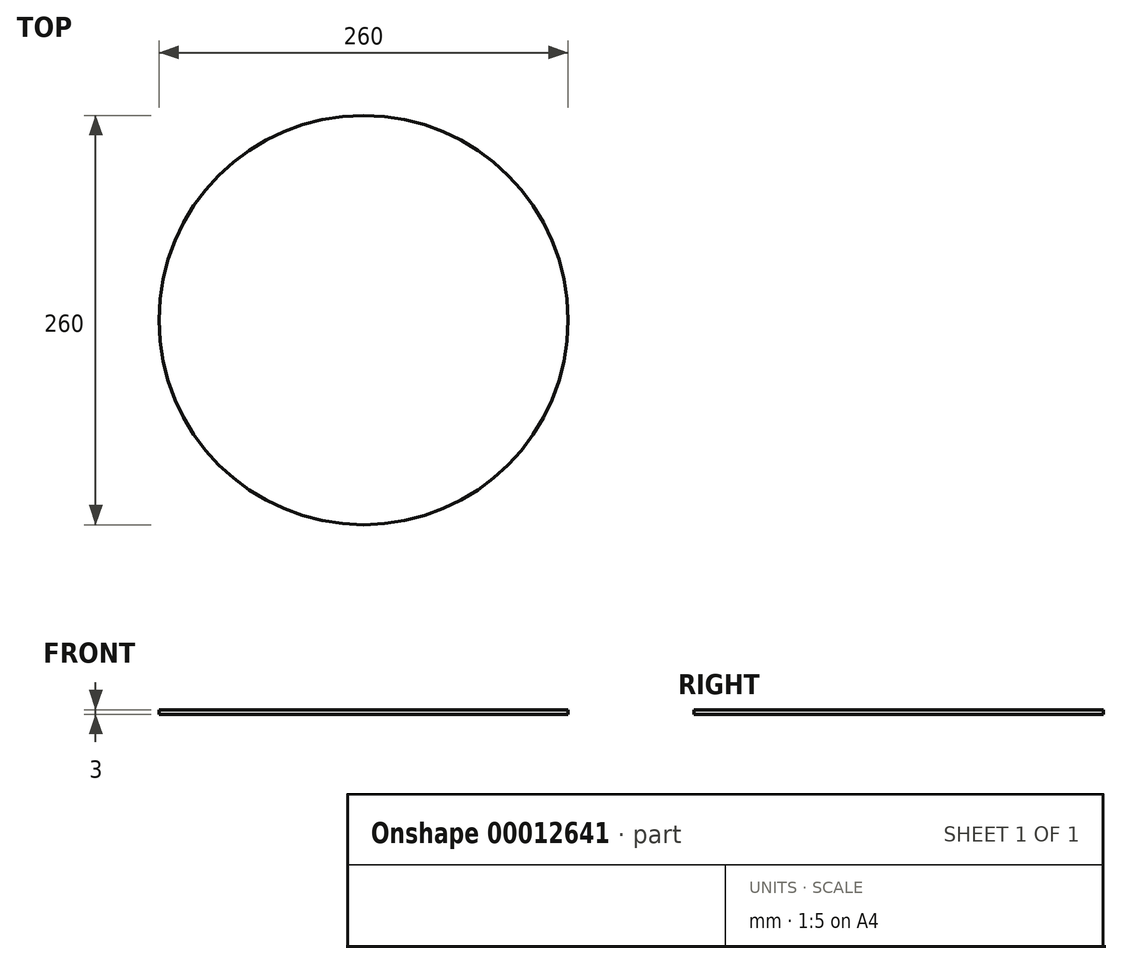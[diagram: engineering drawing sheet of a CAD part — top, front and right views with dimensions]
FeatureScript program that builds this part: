
annotation { "Feature Type Name" : "Feature", "Feature Type Description" : "" }
export const myFeature = defineFeature(function(context is Context, id is Id, definition is map)
    precondition{}
    {
        {
            var Q0;
            Q0=qCreatedBy(makeId("Top.planeOp"),FACE);
            var sketch = newSketch(context, id + "F0", { "sketchPlane" : qUnion([Q0])});
            skCircle(sketch, "E0", {"center": v(0, 0) * mm, "radius": 130 * mm});
            skSolve(sketch);
        }
        {
            var Q0;
            Q0 = qSketchRegion(id + "F0", true);
            extrude(context, id + "F1", {"entities" : qUnion([Q0]), "depth" : 3 * mm});
        }
    });
